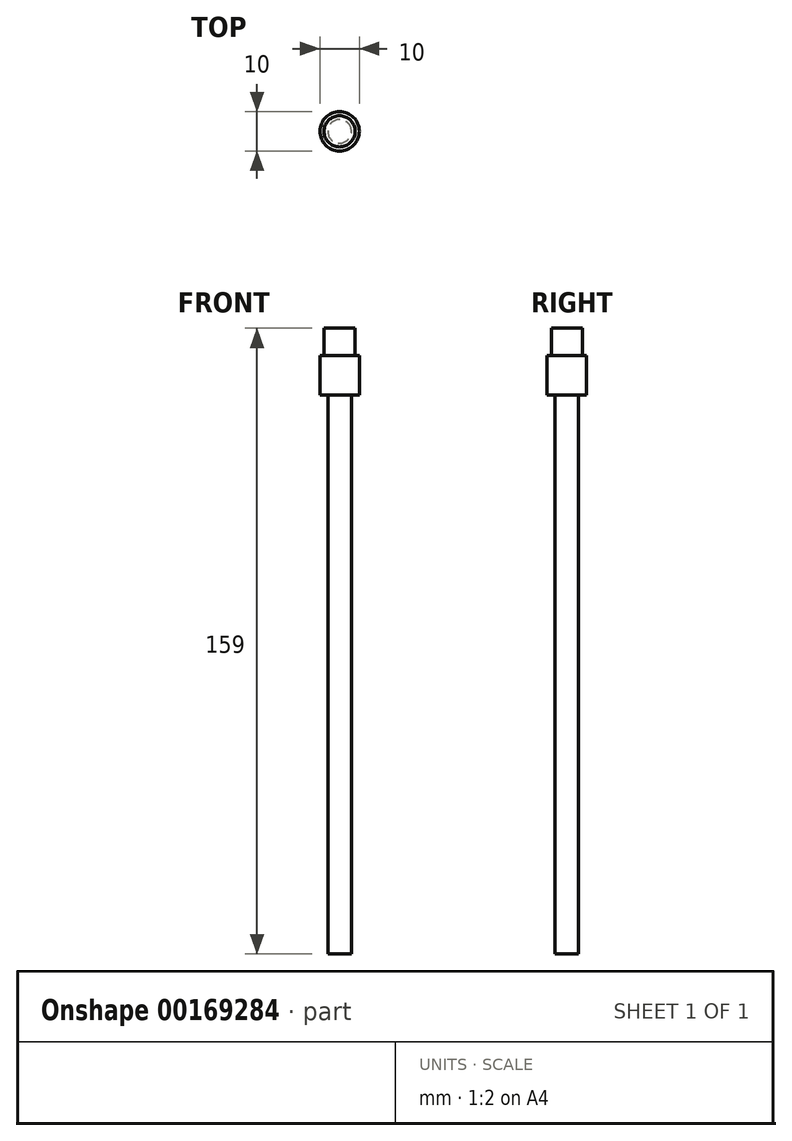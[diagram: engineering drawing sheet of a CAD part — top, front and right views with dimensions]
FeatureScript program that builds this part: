
annotation { "Feature Type Name" : "Feature", "Feature Type Description" : "" }
export const myFeature = defineFeature(function(context is Context, id is Id, definition is map)
    precondition{}
    {
        {
            var Q0;
            Q0=qCreatedBy(makeId("Top.planeOp"),FACE);
            var sketch = newSketch(context, id + "F0", { "sketchPlane" : qUnion([Q0])});
            skCircle(sketch, "E0", {"center": v(0, 0) * mm, "radius": 3 * mm});
            skSolve(sketch);
        }
        {
            var Q0;
            Q0=makeQuery(id+"F0.imprint","IMPRINT",FACE,{"disambiguationData":[TD([[makeQuery(id+"F0.imprint","IMPRINT",EDGE,{"derivedFrom":sQuery(id+"F0.wireOp",EDGE,"E0")}),1.0]])]});
            extrude(context, id + "F1", {"entities" : qUnion([Q0]), "depth" : 150 * mm});
        }
        {
            var Q0;
            Q0=makeQuery(id+"F1.opExtrude","CAP_FACE",FACE,{"disambiguationData":[OSD([sQuery(id+"F0.wireOp",EDGE,"E0")])],"isStart":false});
            var sketch = newSketch(context, id + "F2", { "sketchPlane" : qUnion([Q0])});
            skCircle(sketch, "E1", {"center": v(0, 0) * mm, "radius": 3 * mm});
            skCircle(sketch, "E2", {"center": v(0, 0) * mm, "radius": 5 * mm});
            skSolve(sketch);
        }
        {
            var Q0;
            Q0=makeQuery(id+"F2.imprint","IMPRINT",FACE,{"disambiguationData":[TD([[makeQuery(id+"F2.imprint","IMPRINT",EDGE,{"derivedFrom":sQuery(id+"F2.wireOp",EDGE,"E2")}),1.0]])]});
            var Q1;
            Q1=makeQuery(id+"F2.imprint","IMPRINT",FACE,{"disambiguationData":[TD([[makeQuery(id+"F2.imprint","IMPRINT",EDGE,{"derivedFrom":sQuery(id+"F2.wireOp",EDGE,"E1")}),-1.0]])]});
            extrude(context, id + "F3", {"entities" : qUnion([Q0, Q1]), "oppositeDirection" : true, "depth" : 8 * mm});
        }
        {
            var Q0;
            Q0=makeQuery(id+"F2.imprint","IMPRINT",FACE,{"disambiguationData":[TD([[makeQuery(id+"F2.imprint","IMPRINT",EDGE,{"derivedFrom":sQuery(id+"F2.wireOp",EDGE,"E1")}),1.0]])]});
            var Q1;
            Q1=makeQuery(id+"F2.imprint","IMPRINT",FACE,{"disambiguationData":[TD([[makeQuery(id+"F2.imprint","IMPRINT",EDGE,{"derivedFrom":sQuery(id+"F2.wireOp",EDGE,"E1")}),-1.0]])]});
            extrude(context, id + "F4", {"entities" : qUnion([Q0, Q1]), "operationType" : NewBodyOperationType.ADD, "depth" : 2 * mm});
        }
        {
            var Q0;
            Q0=makeQuery(id+"F4.opExtrude","CAP_FACE",FACE,{"disambiguationData":[OSD([sQuery(id+"F2.wireOp",EDGE,"E2")])],"isStart":false});
            var sketch = newSketch(context, id + "F5", { "sketchPlane" : qUnion([Q0])});
            skCircle(sketch, "E3", {"center": v(0, 0) * mm, "radius": 3.95 * mm});
            skSolve(sketch);
        }
        {
            var Q0;
            Q0=makeQuery(id+"F5.imprint","IMPRINT",FACE,{"disambiguationData":[TD([[makeQuery(id+"F5.imprint","IMPRINT",EDGE,{"derivedFrom":sQuery(id+"F5.wireOp",EDGE,"E3")}),1.0]])]});
            extrude(context, id + "F6", {"entities" : qUnion([Q0]), "operationType" : NewBodyOperationType.ADD, "depth" : 7 * mm});
        }
    });
